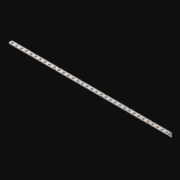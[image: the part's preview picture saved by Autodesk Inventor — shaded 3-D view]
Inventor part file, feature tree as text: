
AUTODESK INVENTOR PART (.ipt)
format: ipt  version: 2021 (Build 250183000, 183)  size: 873,984 bytes
history: native  units: in
note: dims shown in document units (in); Inventor stores cm internally (conversion verified against a paired STEP export)
features: extrude x69, other x68, sketch x3, pattern_linear x1, sheet_metal_op x1
ambient origin geometry x8: Origin, YZ Plane, XZ Plane, XY Plane, X Axis, Y Axis, Z Axis, Center Point
bodies: Solid1 (feature_tree)
feature tree (142):
  pattern_linear  "Rectangular Pattern1"  Spacing1=0.063in  [1 undecoded]
  extrude  "Extrusion1"  Depth=0.5in
  sketch  "Sketch1"  dims[d0=0.182in]
  other  "Srf1"
  sketch  "Sketch2"  dims[d1=0.063in d2=0.0in]
  other  "Srf2"
  other  "Srf3"
  other  "Srf5"
  other  "Srf7"
  other  "Srf9"
  other  "Srf11"
  other  "Srf13"
  other  "Srf15"
  other  "Srf17"
  other  "Srf19"
  other  "Srf21"
  other  "Srf23"
  other  "Srf25"
  other  "Srf27"
  other  "Srf29"
  other  "Srf31"
  other  "Srf33"
  other  "Srf35"
  other  "Srf37"
  other  "Srf39"
  other  "Srf41"
  other  "Srf43"
  other  "Srf45"
  other  "Srf47"
  other  "Srf49"
  other  "Srf51"
  other  "Srf53"
  other  "Srf55"
  other  "Srf57"
  other  "Srf59"
  other  "Srf61"
  other  "Srf63"
  other  "Srf65"
  other  "Srf67"
  other  "Srf4"
  other  "Srf6"
  other  "Srf8"
  other  "Srf10"
  other  "Srf12"
  other  "Srf14"
  other  "Srf16"
  other  "Srf18"
  other  "Srf20"
  other  "Srf22"
  other  "Srf24"
  other  "Srf26"
  other  "Srf28"
  other  "Srf30"
  other  "Srf32"
  other  "Srf34"
  other  "Srf36"
  other  "Srf38"
  other  "Srf40"
  other  "Srf42"
  other  "Srf44"
  other  "Srf46"
  other  "Srf48"
  other  "Srf50"
  other  "Srf52"
  other  "Srf54"
  other  "Srf56"
  other  "Srf58"
  other  "Srf60"
  other  "Srf62"
  other  "Srf64"
  other  "Srf66"
  other  "Srf68"
  sketch  "Sketch3"  dims[d3=0.182in d4=0.063in d5=0.0in d8=0.5in d9=0.5in d10=0.0in]
  sheet_metal_op  "Fold1"
  extrude  "ExtrusionSrf1"  Depth=0.5in TaperAngle=0.0deg
  extrude  "ExtrusionSrf2"  [1 undecoded]
  extrude  "ExtrusionSrf3"  [1 undecoded]
  extrude  "ExtrusionSrf4"  [1 undecoded]
  extrude  "ExtrusionSrf5"  [1 undecoded]
  extrude  "ExtrusionSrf6"  [1 undecoded]
  extrude  "ExtrusionSrf7"  [1 undecoded]
  extrude  "ExtrusionSrf8"  [1 undecoded]
  extrude  "ExtrusionSrf9"  [1 undecoded]
  extrude  "ExtrusionSrf10"  [1 undecoded]
  extrude  "ExtrusionSrf11"  [1 undecoded]
  extrude  "ExtrusionSrf12"  [1 undecoded]
  extrude  "ExtrusionSrf13"  [1 undecoded]
  extrude  "ExtrusionSrf14"  [1 undecoded]
  extrude  "ExtrusionSrf15"  [1 undecoded]
  extrude  "ExtrusionSrf16"  [1 undecoded]
  extrude  "ExtrusionSrf17"  [1 undecoded]
  extrude  "ExtrusionSrf18"  [1 undecoded]
  extrude  "ExtrusionSrf19"  [1 undecoded]
  extrude  "ExtrusionSrf20"  [1 undecoded]
  extrude  "ExtrusionSrf21"  [1 undecoded]
  extrude  "ExtrusionSrf22"  [1 undecoded]
  extrude  "ExtrusionSrf23"  [1 undecoded]
  extrude  "ExtrusionSrf24"  [1 undecoded]
  extrude  "ExtrusionSrf25"  [1 undecoded]
  extrude  "ExtrusionSrf26"  [1 undecoded]
  extrude  "ExtrusionSrf27"  [1 undecoded]
  extrude  "ExtrusionSrf28"  [1 undecoded]
  extrude  "ExtrusionSrf29"  [1 undecoded]
  extrude  "ExtrusionSrf30"  [1 undecoded]
  extrude  "ExtrusionSrf31"  [1 undecoded]
  extrude  "ExtrusionSrf32"  [1 undecoded]
  extrude  "ExtrusionSrf33"  [1 undecoded]
  extrude  "ExtrusionSrf34"  [1 undecoded]
  extrude  "ExtrusionSrf35"  [1 undecoded]
  extrude  "ExtrusionSrf37"  [1 undecoded]
  extrude  "ExtrusionSrf38"  [1 undecoded]
  extrude  "ExtrusionSrf39"  [1 undecoded]
  extrude  "ExtrusionSrf40"  [1 undecoded]
  extrude  "ExtrusionSrf41"  [1 undecoded]
  extrude  "ExtrusionSrf42"  [1 undecoded]
  extrude  "ExtrusionSrf43"  [1 undecoded]
  extrude  "ExtrusionSrf44"  [1 undecoded]
  extrude  "ExtrusionSrf45"  [1 undecoded]
  extrude  "ExtrusionSrf46"  [1 undecoded]
  extrude  "ExtrusionSrf47"  [1 undecoded]
  extrude  "ExtrusionSrf48"  [1 undecoded]
  extrude  "ExtrusionSrf49"  [1 undecoded]
  extrude  "ExtrusionSrf50"  [1 undecoded]
  extrude  "ExtrusionSrf51"  [1 undecoded]
  extrude  "ExtrusionSrf52"  [1 undecoded]
  extrude  "ExtrusionSrf53"  [1 undecoded]
  extrude  "ExtrusionSrf54"  [1 undecoded]
  extrude  "ExtrusionSrf55"  [1 undecoded]
  extrude  "ExtrusionSrf56"  [1 undecoded]
  extrude  "ExtrusionSrf57"  [1 undecoded]
  extrude  "ExtrusionSrf58"  [1 undecoded]
  extrude  "ExtrusionSrf59"  [1 undecoded]
  extrude  "ExtrusionSrf60"  [1 undecoded]
  extrude  "ExtrusionSrf61"  [1 undecoded]
  extrude  "ExtrusionSrf62"  [1 undecoded]
  extrude  "ExtrusionSrf63"  [1 undecoded]
  extrude  "ExtrusionSrf64"  [1 undecoded]
  extrude  "ExtrusionSrf65"  [1 undecoded]
  extrude  "ExtrusionSrf66"  [1 undecoded]
  extrude  "ExtrusionSrf67"  [1 undecoded]
  extrude  "ExtrusionSrf68"  [1 undecoded]
  extrude  "ExtrusionSrf69"  [1 undecoded]
note: 68 required parameter values undecoded (feature->parameter linkage not recoverable at this tier; creation-order binding heuristic only, values carry confidence <= 0.55)
